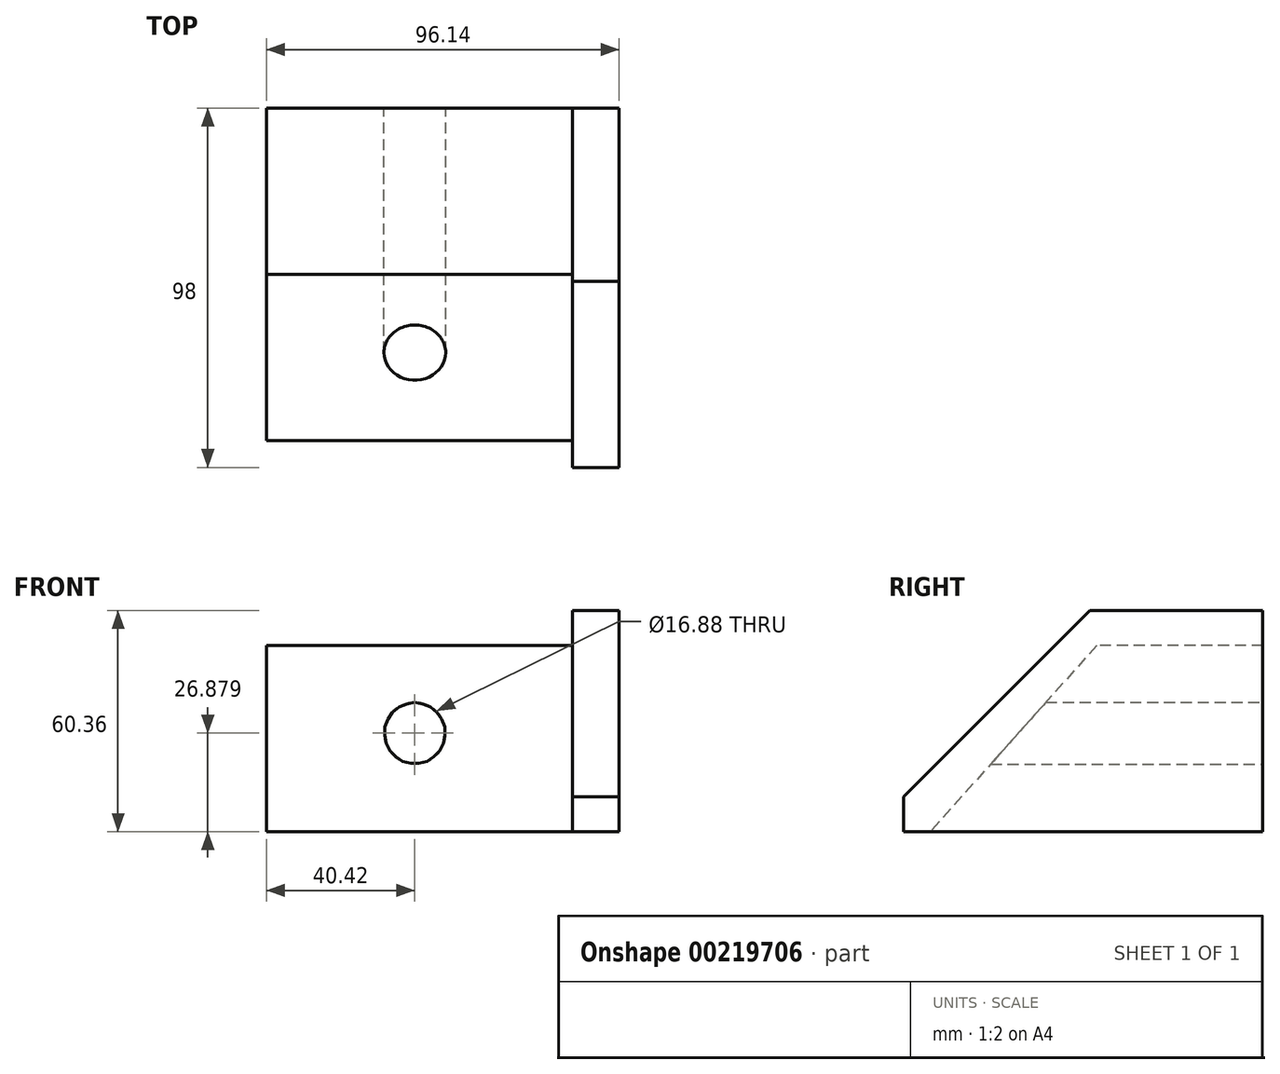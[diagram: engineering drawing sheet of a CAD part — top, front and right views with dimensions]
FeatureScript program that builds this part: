
annotation { "Feature Type Name" : "Feature", "Feature Type Description" : "" }
export const myFeature = defineFeature(function(context is Context, id is Id, definition is map)
    precondition{}
    {
        {
            var Q0;
            Q0=qCreatedBy(makeId("Top.planeOp"),FACE);
            var sketch = newSketch(context, id + "F0", { "sketchPlane" : qUnion([Q0])});
            skLineSegment(sketch, "E0.bottom", {"start": v(43.02, 45.34) * mm, "end": v(-40.42, 45.34) * mm});
            skLineSegment(sketch, "E0.top", {"start": v(43.02, -45.34) * mm, "end": v(-40.42, -45.34) * mm});
            skLineSegment(sketch, "E0.left", {"start": v(43.02, 45.34) * mm, "end": v(43.02, -45.34) * mm});
            skLineSegment(sketch, "E0.right", {"start": v(-40.42, 45.34) * mm, "end": v(-40.42, -45.34) * mm});
            skPoint(sketch, "E0.middle", {"position": v(1.3, 0) * mm});
            skSolve(sketch);
        }
        {
            var Q0;
            Q0=makeQuery(id+"F0.imprint","IMPRINT",FACE,{"disambiguationData":[TD([[makeQuery(id+"F0.imprint","IMPRINT",EDGE,{"derivedFrom":sQuery(id+"F0.wireOp",EDGE,"E0.bottom")}),1.0]])]});
            extrude(context, id + "F1", {"entities" : qUnion([Q0]), "depth" : 50.8 * mm});
        }
        {
            var Q0;
            Q0=makeQuery(id+"F1.opExtrude","SWEPT_FACE",FACE,{"disambiguationData":[OSD([sQuery(id+"F0.wireOp",EDGE,"E0.right")])]});
            var sketch = newSketch(context, id + "F2", { "sketchPlane" : qUnion([Q0])});
            skLineSegment(sketch, "E1.0", {"start": v(-45.34, 50.8) * mm, "end": v(45.34, 50.8) * mm});
            skLineSegment(sketch, "E2.0", {"start": v(45.34, 50.8) * mm, "end": v(45.34, 0) * mm});
            skLineSegment(sketch, "E3", {"start": v(0, 50.8) * mm, "end": v(45.34, 0) * mm});
            skSolve(sketch);
        }
        {
            var Q0;
            {var subQ0=sQuery(id+"F2.wireOp",EDGE,"E2.0");Q0=makeQuery(id+"F2.imprint","IMPRINT",FACE,{"disambiguationData":[TD([[makeQuery(id+"F2.imprint","IMPRINT",EDGE,{"derivedFrom":subQ0}),-1.0]])]});}
            extrude(context, id + "F3", {"entities" : qUnion([Q0]), "operationType" : NewBodyOperationType.REMOVE, "endBound" : BoundingType.THROUGH_ALL, "oppositeDirection" : true, "depth" : 25.4 * mm});
        }
        {
            var Q0;
            Q0=makeQuery(id+"F1.opExtrude","SWEPT_FACE",FACE,{"disambiguationData":[OSD([sQuery(id+"F0.wireOp",EDGE,"E0.bottom")])]});
            var sketch = newSketch(context, id + "F4", { "sketchPlane" : qUnion([Q0])});
            skCircle(sketch, "E4", {"center": v(0, 26.88) * mm, "radius": 8.44 * mm});
            skSolve(sketch);
        }
        {
            var Q0;
            Q0=makeQuery(id+"F4.imprint","IMPRINT",FACE,{"disambiguationData":[TD([[makeQuery(id+"F4.imprint","IMPRINT",EDGE,{"derivedFrom":sQuery(id+"F4.wireOp",EDGE,"E4")}),1.0]])]});
            extrude(context, id + "F5", {"entities" : qUnion([Q0]), "operationType" : NewBodyOperationType.REMOVE, "endBound" : BoundingType.THROUGH_ALL, "oppositeDirection" : true, "depth" : 50.8 * mm});
        }
        {
            var Q0;
            Q0=makeQuery(id+"F1.opExtrude","SWEPT_FACE",FACE,{"disambiguationData":[OSD([sQuery(id+"F0.wireOp",EDGE,"E0.left")])]});
            var sketch = newSketch(context, id + "F6", { "sketchPlane" : qUnion([Q0])});
            skLineSegment(sketch, "E5.bottom", {"start": v(45.34, 0) * mm, "end": v(-52.66, 0) * mm});
            skLineSegment(sketch, "E5.top", {"start": v(45.34, 0) * mm, "end": v(-52.66, 0) * mm});
            skLineSegment(sketch, "E5.left", {"start": v(45.34, 0) * mm, "end": v(45.34, 0) * mm});
            skLineSegment(sketch, "E5.right", {"start": v(-52.66, 0) * mm, "end": v(-52.66, 0) * mm});
            skLineSegment(sketch, "E6.top", {"start": v(45.34, 60.36) * mm, "end": v(-52.66, 60.36) * mm});
            skLineSegment(sketch, "E6.left", {"start": v(45.34, 0) * mm, "end": v(45.34, 60.36) * mm});
            skLineSegment(sketch, "E6.right", {"start": v(-52.66, 0) * mm, "end": v(-52.66, 60.36) * mm});
            skSolve(sketch);
        }
        {
            var Q0;
            {var subQ3=sQuery(id+"F0.wireOp",EDGE,"E0.left");var subQ5=makeQuery(id+"F1.opExtrude","CAP_EDGE",EDGE,{"disambiguationData":[OSD([subQ3])],"isStart":false});Q0=makeQuery(id+"F6.imprint","IMPRINT",FACE,{"disambiguationData":[TD([[makeQuery(id+"F6.imprint","IMPRINT",EDGE,{"derivedFrom":subQ5}),1.0]])]});}
            var Q1;
            {var subQ3=sQuery(id+"F6.wireOp",EDGE,"E6.top");Q1=makeQuery(id+"F6.imprint","IMPRINT",FACE,{"disambiguationData":[TD([[makeQuery(id+"F6.imprint","IMPRINT",EDGE,{"derivedFrom":subQ3}),1.0]])]});}
            extrude(context, id + "F7", {"entities" : qUnion([Q0, Q1]), "operationType" : NewBodyOperationType.ADD, "depth" : 12.7 * mm});
        }
        {
            var Q0;
            Q0=makeQuery(id+"F7.opExtrude","SWEPT_EDGE",EDGE,{"disambiguationData":[OSD([sQuery(id+"F6.wireOp",EDGE,"E6.top"),sQuery(id+"F6.wireOp",EDGE,"E6.right")])]});
            chamfer(context, id + "F8", {"entities" : qUnion([Q0]), "width" : 50.8 * mm, "tangentPropagation" : true});
        }
    });
